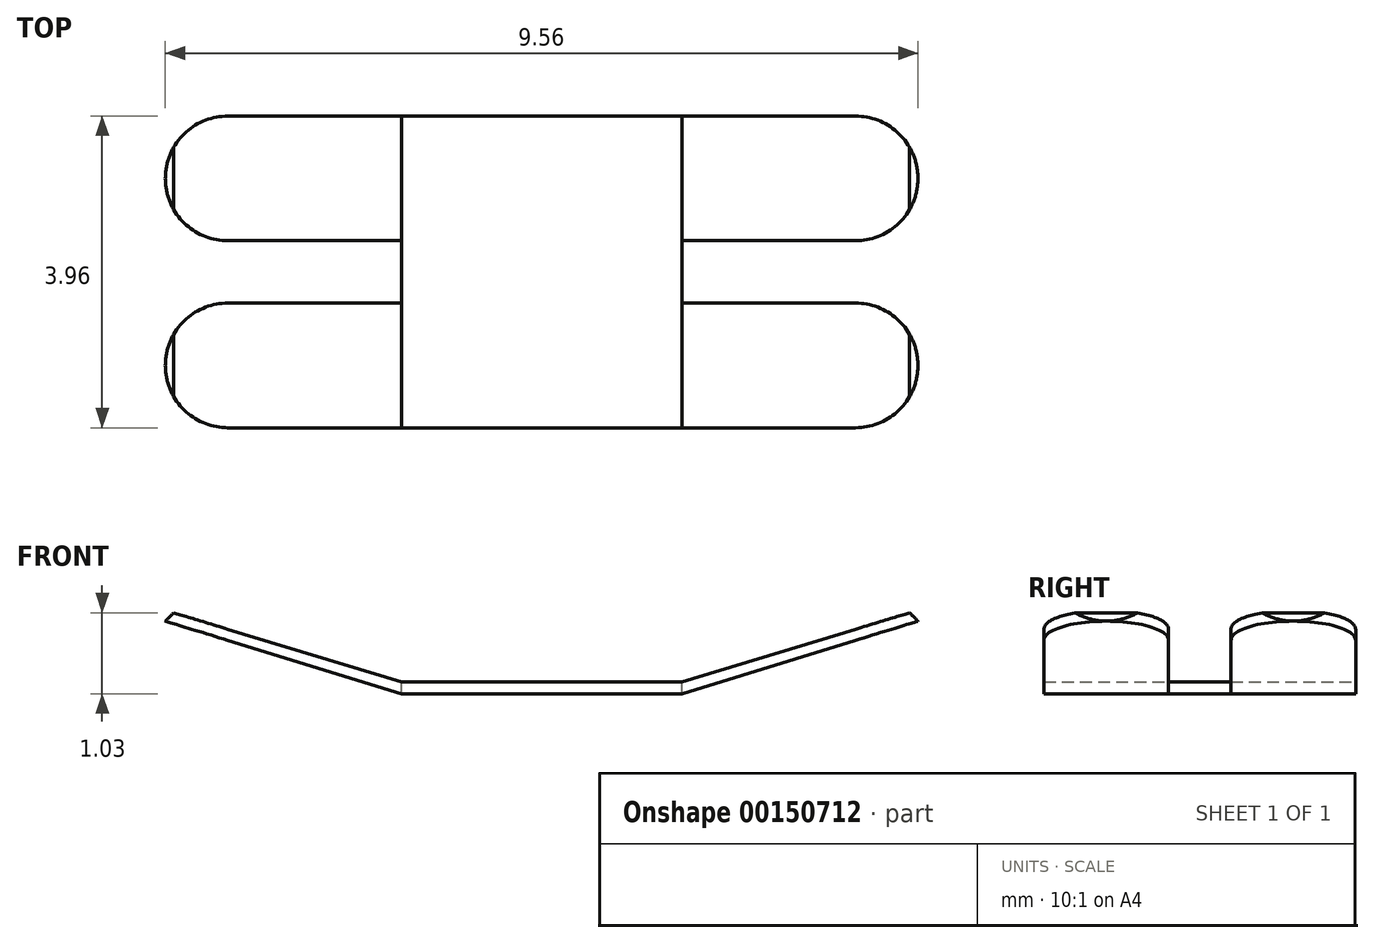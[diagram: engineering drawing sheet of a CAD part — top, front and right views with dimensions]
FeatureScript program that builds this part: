
annotation { "Feature Type Name" : "Feature", "Feature Type Description" : "" }
export const myFeature = defineFeature(function(context is Context, id is Id, definition is map)
    precondition{}
    {
        {
            var Q0;
            Q0=qCreatedBy(makeId("Front.planeOp"),FACE);
            var sketch = newSketch(context, id + "F0", { "sketchPlane" : qUnion([Q0])});
            skLineSegment(sketch, "E0.top", {"start": v(-1.78, 0) * mm, "end": v(1.78, 0) * mm});
            skLineSegment(sketch, "E1.bottom", {"start": v(-1.78, 0.15) * mm, "end": v(1.78, 0.15) * mm});
            skLineSegment(sketch, "E1.left", {"start": v(-1.78, 0.15) * mm, "end": v(-1.78, 0) * mm});
            skLineSegment(sketch, "E1.right", {"start": v(1.78, 0.15) * mm, "end": v(1.78, 0) * mm});
            skLineSegment(sketch, "E2", {"start": v(-4.67, 1.03) * mm, "end": v(-4.78, 0.92) * mm});
            skLineSegment(sketch, "E3", {"start": v(-4.67, 1.03) * mm, "end": v(-1.78, 0.15) * mm});
            skLineSegment(sketch, "E4", {"start": v(-1.78, 0) * mm, "end": v(-4.78, 0.92) * mm});
            skLineSegment(sketch, "E5", {"start": v(4.67, 1.03) * mm, "end": v(4.78, 0.92) * mm});
            skLineSegment(sketch, "E6", {"start": v(1.78, 0) * mm, "end": v(4.78, 0.92) * mm});
            skLineSegment(sketch, "E7", {"start": v(4.67, 1.03) * mm, "end": v(1.78, 0.15) * mm});
            skSolve(sketch);
        }
        {
            var Q0;
            Q0 = qSketchRegion(id + "F0", true);
            extrude(context, id + "F1", {"entities" : qUnion([Q0]), "depth" : 1.98 * mm, "hasSecondDirection" : true, "secondDirectionOppositeDirection" : true, "secondDirectionDepth" : 1.98 * mm});
        }
        {
            var Q0;
            Q0=makeQuery(id+"F1.opExtrude","SWEPT_FACE",FACE,{"disambiguationData":[OSD([sQuery(id+"F0.wireOp",EDGE,"E1.bottom")])]});
            var sketch = newSketch(context, id + "F2", { "sketchPlane" : qUnion([Q0])});
            skPoint(sketch, "E8.endSnap0", {"position": v(-4.78, 1.19) * mm});
            skArc(sketch, "E9", {"start": v(-3.99, 1.98) * mm, "mid": v(-4.55, 1.75) * mm, "end": v(-4.78, 1.19) * mm});
            skArc(sketch, "E10", {"start": v(-4.78, 1.19) * mm, "mid": v(-4.55, 0.63) * mm, "end": v(-3.99, 0.4) * mm});
            skLineSegment(sketch, "E11", {"start": v(-3.99, 0.4) * mm, "end": v(-1.78, 0.4) * mm});
            skLineSegment(sketch, "E12", {"start": v(-1.78, 0.4) * mm, "end": v(-1.78, 0) * mm});
            skLineSegment(sketch, "E13.MirrorCS", {"start": v(-1.78, -0.4) * mm, "end": v(-1.78, 0) * mm});
            skLineSegment(sketch, "E14.MirrorCS", {"start": v(-3.99, -0.4) * mm, "end": v(-1.78, -0.4) * mm});
            skArc(sketch, "E15.MirrorCS", {"start": v(-4.78, -1.19) * mm, "mid": v(-4.55, -0.63) * mm, "end": v(-3.99, -0.4) * mm});
            skPoint(sketch, "E16.MirrorP", {"position": v(-4.78, -1.19) * mm});
            skArc(sketch, "E17.MirrorCS", {"start": v(-3.99, -1.98) * mm, "mid": v(-4.55, -1.75) * mm, "end": v(-4.78, -1.19) * mm});
            skLineSegment(sketch, "E18", {"start": v(-3.99, -1.98) * mm, "end": v(-3.99, -2.3) * mm});
            skLineSegment(sketch, "E19", {"start": v(-3.99, -2.3) * mm, "end": v(-5.45, -2.3) * mm});
            skLineSegment(sketch, "E20", {"start": v(-5.45, -2.3) * mm, "end": v(-5.45, 2.37) * mm});
            skLineSegment(sketch, "E21", {"start": v(-5.45, 2.37) * mm, "end": v(-3.98, 2.37) * mm});
            skLineSegment(sketch, "E22", {"start": v(-3.98, 2.37) * mm, "end": v(-3.99, 1.98) * mm});
            skArc(sketch, "E23.MirrorCS", {"start": v(4.78, -1.19) * mm, "mid": v(4.55, -0.63) * mm, "end": v(3.99, -0.4) * mm});
            skLineSegment(sketch, "E24.MirrorCS", {"start": v(3.99, -0.4) * mm, "end": v(1.78, -0.4) * mm});
            skArc(sketch, "E25.MirrorCS", {"start": v(3.99, -1.98) * mm, "mid": v(4.55, -1.75) * mm, "end": v(4.78, -1.19) * mm});
            skLineSegment(sketch, "E26.MirrorCS", {"start": v(1.78, -0.4) * mm, "end": v(1.78, 0) * mm});
            skLineSegment(sketch, "E27.MirrorCS", {"start": v(3.99, 0.4) * mm, "end": v(1.78, 0.4) * mm});
            skLineSegment(sketch, "E28.MirrorCS", {"start": v(3.99, -2.3) * mm, "end": v(5.45, -2.3) * mm});
            skPoint(sketch, "E29.MirrorP", {"position": v(4.78, -1.19) * mm});
            skLineSegment(sketch, "E30.MirrorCS", {"start": v(5.45, -2.3) * mm, "end": v(5.45, 2.37) * mm});
            skLineSegment(sketch, "E31.MirrorCS", {"start": v(1.78, 0.4) * mm, "end": v(1.78, 0) * mm});
            skPoint(sketch, "E32.MirrorP", {"position": v(4.78, 1.19) * mm});
            skArc(sketch, "E33.MirrorCS", {"start": v(4.78, 1.19) * mm, "mid": v(4.55, 0.63) * mm, "end": v(3.99, 0.4) * mm});
            skLineSegment(sketch, "E34.MirrorCS", {"start": v(5.45, 2.37) * mm, "end": v(3.98, 2.37) * mm});
            skLineSegment(sketch, "E35.MirrorCS", {"start": v(3.99, -1.98) * mm, "end": v(3.99, -2.3) * mm});
            skLineSegment(sketch, "E36.MirrorCS", {"start": v(3.98, 2.37) * mm, "end": v(3.99, 1.98) * mm});
            skArc(sketch, "E37.MirrorCS", {"start": v(3.99, 1.98) * mm, "mid": v(4.55, 1.75) * mm, "end": v(4.78, 1.19) * mm});
            skSolve(sketch);
        }
        {
            var Q0;
            Q0 = qSketchRegion(id + "F2", true);
            extrude(context, id + "F3", {"entities" : qUnion([Q0]), "operationType" : NewBodyOperationType.REMOVE, "depth" : 25 * mm});
        }
        {
            var Q0;
            Q0=makeQuery(id+"F3.boolean.opBoolean","MERGE",FACE,{"derivedFrom":[makeQuery(id+"F1.opExtrude","SWEPT_FACE",FACE,{"disambiguationData":[OSD([sQuery(id+"F0.wireOp",EDGE,"E1.bottom")])]}),makeQuery(id+"F3.opExtrude","CAP_FACE",FACE,{"disambiguationData":[OSD([sQuery(id+"F2.wireOp",EDGE,"E9"),sQuery(id+"F2.wireOp",EDGE,"E10"),sQuery(id+"F2.wireOp",EDGE,"E11"),sQuery(id+"F2.wireOp",EDGE,"E12"),sQuery(id+"F2.wireOp",EDGE,"E13.MirrorCS"),sQuery(id+"F2.wireOp",EDGE,"E14.MirrorCS"),sQuery(id+"F2.wireOp",EDGE,"E15.MirrorCS"),sQuery(id+"F2.wireOp",EDGE,"E17.MirrorCS"),sQuery(id+"F2.wireOp",EDGE,"E18"),sQuery(id+"F2.wireOp",EDGE,"E19"),sQuery(id+"F2.wireOp",EDGE,"E20"),sQuery(id+"F2.wireOp",EDGE,"E21"),sQuery(id+"F2.wireOp",EDGE,"E22")])],"isStart":true}),makeQuery(id+"F3.opExtrude","CAP_FACE",FACE,{"disambiguationData":[OSD([sQuery(id+"F2.wireOp",EDGE,"E23.MirrorCS"),sQuery(id+"F2.wireOp",EDGE,"E24.MirrorCS"),sQuery(id+"F2.wireOp",EDGE,"E25.MirrorCS"),sQuery(id+"F2.wireOp",EDGE,"E26.MirrorCS"),sQuery(id+"F2.wireOp",EDGE,"E27.MirrorCS"),sQuery(id+"F2.wireOp",EDGE,"E28.MirrorCS"),sQuery(id+"F2.wireOp",EDGE,"E30.MirrorCS"),sQuery(id+"F2.wireOp",EDGE,"E31.MirrorCS"),sQuery(id+"F2.wireOp",EDGE,"E33.MirrorCS"),sQuery(id+"F2.wireOp",EDGE,"E34.MirrorCS"),sQuery(id+"F2.wireOp",EDGE,"E35.MirrorCS"),sQuery(id+"F2.wireOp",EDGE,"E36.MirrorCS"),sQuery(id+"F2.wireOp",EDGE,"E37.MirrorCS")])],"isStart":true})]});
            var sketch = newSketch(context, id + "F4", { "sketchPlane" : qUnion([Q0])});
            skLineSegment(sketch, "E38.bottom", {"start": v(-1.78, 0.4) * mm, "end": v(-3.05, 0.4) * mm});
            skLineSegment(sketch, "E38.top", {"start": v(-1.78, -0.4) * mm, "end": v(-3.05, -0.4) * mm});
            skLineSegment(sketch, "E38.left", {"start": v(-1.78, 0.4) * mm, "end": v(-1.78, -0.4) * mm});
            skLineSegment(sketch, "E38.right", {"start": v(-3.05, 0.4) * mm, "end": v(-3.05, -0.4) * mm});
            skLineSegment(sketch, "E39.MirrorCS", {"start": v(3.05, 0.4) * mm, "end": v(3.05, -0.4) * mm});
            skLineSegment(sketch, "E40.MirrorCS", {"start": v(1.78, 0.4) * mm, "end": v(1.78, -0.4) * mm});
            skLineSegment(sketch, "E41.MirrorCS", {"start": v(1.78, 0.4) * mm, "end": v(3.05, 0.4) * mm});
            skLineSegment(sketch, "E42.MirrorCS", {"start": v(1.78, -0.4) * mm, "end": v(3.05, -0.4) * mm});
            skSolve(sketch);
        }
        {
            var Q0;
            Q0 = qSketchRegion(id + "F4", true);
            extrude(context, id + "F5", {"entities" : qUnion([Q0]), "operationType" : NewBodyOperationType.REMOVE, "oppositeDirection" : true, "depth" : 25 * mm});
        }
    });
